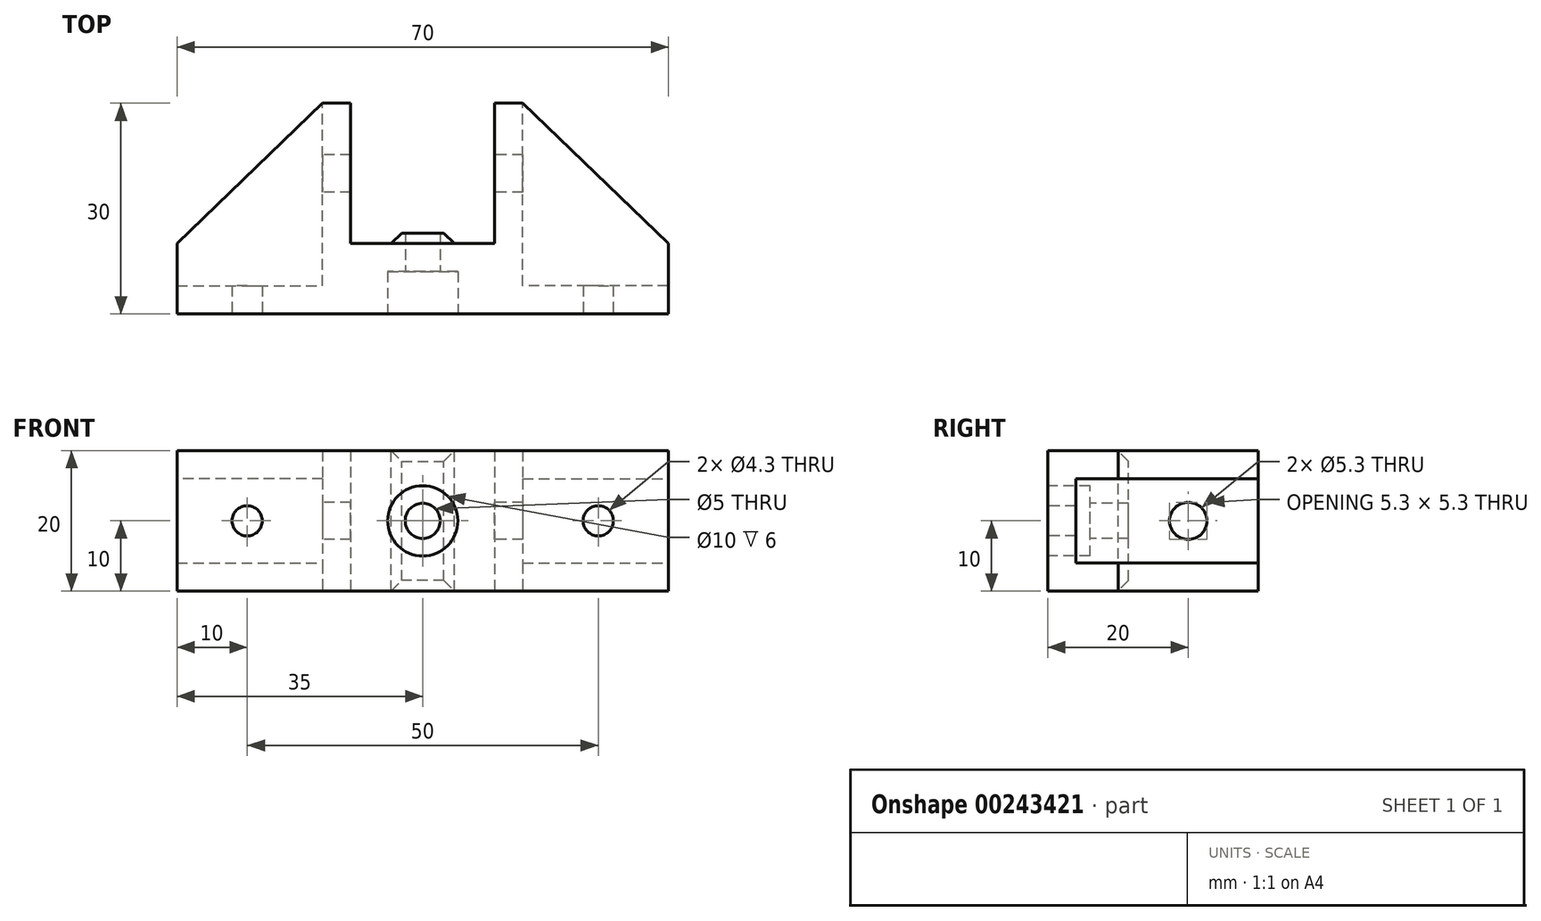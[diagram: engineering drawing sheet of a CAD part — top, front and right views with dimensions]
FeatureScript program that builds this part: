
annotation { "Feature Type Name" : "Feature", "Feature Type Description" : "" }
export const myFeature = defineFeature(function(context is Context, id is Id, definition is map)
    precondition{}
    {
        {
            var Q0;
            Q0=qCreatedBy(makeId("Top.planeOp"),FACE);
            var sketch = newSketch(context, id + "F0", { "sketchPlane" : qUnion([Q0])});
            skLineSegment(sketch, "E0.bottom", {"start": v(0, 0) * mm, "end": v(70, 0) * mm});
            skLineSegment(sketch, "E0.top", {"start": v(0, 10) * mm, "end": v(20.75, 10) * mm});
            skLineSegment(sketch, "E0.left", {"start": v(0, 0) * mm, "end": v(0, 10) * mm});
            skLineSegment(sketch, "E0.right", {"start": v(70, 0) * mm, "end": v(70, 10) * mm});
            skLineSegment(sketch, "E1.top", {"start": v(20.75, 30) * mm, "end": v(24.75, 30) * mm});
            skLineSegment(sketch, "E1.left", {"start": v(20.75, 10) * mm, "end": v(20.75, 30) * mm});
            skLineSegment(sketch, "E1.right", {"start": v(49.25, 10) * mm, "end": v(49.25, 30) * mm});
            skLineSegment(sketch, "E2.trimOffspring", {"start": v(49.25, 10) * mm, "end": v(70, 10) * mm});
            skLineSegment(sketch, "E3.top", {"start": v(24.75, 10) * mm, "end": v(45.25, 10) * mm});
            skLineSegment(sketch, "E3.left", {"start": v(24.75, 30) * mm, "end": v(24.75, 10) * mm});
            skLineSegment(sketch, "E3.right", {"start": v(45.25, 30) * mm, "end": v(45.25, 10) * mm});
            skLineSegment(sketch, "E4.trimOffspring", {"start": v(45.25, 30) * mm, "end": v(49.25, 30) * mm});
            skSolve(sketch);
        }
        {
            var Q0;
            Q0 = qSketchRegion(id + "F0", true);
            extrude(context, id + "F1", {"entities" : qUnion([Q0]), "depth" : 20 * mm});
        }
        {
            var Q0;
            Q0=makeQuery(id+"F1.opExtrude","CAP_FACE",FACE,{"disambiguationData":[OSD([sQuery(id+"F0.wireOp",EDGE,"E0.bottom"),sQuery(id+"F0.wireOp",EDGE,"E0.top"),sQuery(id+"F0.wireOp",EDGE,"E0.left"),sQuery(id+"F0.wireOp",EDGE,"E0.right"),sQuery(id+"F0.wireOp",EDGE,"E1.top"),sQuery(id+"F0.wireOp",EDGE,"E1.left"),sQuery(id+"F0.wireOp",EDGE,"E1.right"),sQuery(id+"F0.wireOp",EDGE,"E2.trimOffspring"),sQuery(id+"F0.wireOp",EDGE,"E3.top"),sQuery(id+"F0.wireOp",EDGE,"E3.left"),sQuery(id+"F0.wireOp",EDGE,"E3.right"),sQuery(id+"F0.wireOp",EDGE,"E4.trimOffspring")])],"isStart":false});
            var sketch = newSketch(context, id + "F2", { "sketchPlane" : qUnion([Q0])});
            skLineSegment(sketch, "E5", {"start": v(30.5, 10) * mm, "end": v(32, 11.5) * mm});
            skLineSegment(sketch, "E6", {"start": v(32, 11.5) * mm, "end": v(38, 11.5) * mm});
            skLineSegment(sketch, "E7", {"start": v(38, 11.5) * mm, "end": v(39.5, 10) * mm});
            skLineSegment(sketch, "E8", {"start": v(39.5, 10) * mm, "end": v(30.5, 10) * mm});
            skSolve(sketch);
        }
        {
            var Q0;
            Q0 = qSketchRegion(id + "F2", true);
            var Q1;
            Q1=makeQuery(id+"F1.opExtrude","CAP_FACE",FACE,{"disambiguationData":[OSD([sQuery(id+"F0.wireOp",EDGE,"E0.bottom"),sQuery(id+"F0.wireOp",EDGE,"E0.top"),sQuery(id+"F0.wireOp",EDGE,"E0.left"),sQuery(id+"F0.wireOp",EDGE,"E0.right"),sQuery(id+"F0.wireOp",EDGE,"E1.top"),sQuery(id+"F0.wireOp",EDGE,"E1.left"),sQuery(id+"F0.wireOp",EDGE,"E1.right"),sQuery(id+"F0.wireOp",EDGE,"E2.trimOffspring"),sQuery(id+"F0.wireOp",EDGE,"E3.top"),sQuery(id+"F0.wireOp",EDGE,"E3.left"),sQuery(id+"F0.wireOp",EDGE,"E3.right"),sQuery(id+"F0.wireOp",EDGE,"E4.trimOffspring")])],"isStart":true});
            extrude(context, id + "F3", {"entities" : qUnion([Q0]), "operationType" : NewBodyOperationType.ADD, "endBound" : BoundingType.UP_TO_SURFACE, "oppositeDirection" : true, "endBoundEntityFace" : qUnion([Q1]), "depth" : 25 * mm});
        }
        {
            var Q0;
            Q0=makeQuery(id+"F1.opExtrude","SWEPT_FACE",FACE,{"disambiguationData":[OSD([sQuery(id+"F0.wireOp",EDGE,"E0.top")])]});
            var sketch = newSketch(context, id + "F4", { "sketchPlane" : qUnion([Q0])});
            skLineSegment(sketch, "E9.bottom", {"start": v(0, 16) * mm, "end": v(-20.75, 16) * mm});
            skLineSegment(sketch, "E9.top", {"start": v(0, 4) * mm, "end": v(-20.75, 4) * mm});
            skLineSegment(sketch, "E9.left", {"start": v(0, 16) * mm, "end": v(0, 4) * mm});
            skLineSegment(sketch, "E9.right", {"start": v(-20.75, 16) * mm, "end": v(-20.75, 4) * mm});
            skLineSegment(sketch, "E10.0.0", {"start": v(-38, 20) * mm, "end": v(-38, 0) * mm, "construction": true});
            skLineSegment(sketch, "E10.0.1", {"start": v(-38, 0) * mm, "end": v(-32, 0) * mm, "construction": true});
            skLineSegment(sketch, "E10.0.2", {"start": v(-32, 0) * mm, "end": v(-32, 20) * mm, "construction": true});
            skLineSegment(sketch, "E10.0.3", {"start": v(-32, 20) * mm, "end": v(-38, 20) * mm, "construction": true});
            skLineSegment(sketch, "E11", {"start": v(-35, 20) * mm, "end": v(-35, 0) * mm, "construction": true});
            skLineSegment(sketch, "E12.MirrorCS", {"start": v(-49.25, 16) * mm, "end": v(-49.25, 4) * mm});
            skLineSegment(sketch, "E13.MirrorCS", {"start": v(-70, 16) * mm, "end": v(-70, 4) * mm});
            skLineSegment(sketch, "E14.MirrorCS", {"start": v(-70, 16) * mm, "end": v(-49.25, 16) * mm});
            skLineSegment(sketch, "E15.MirrorCS", {"start": v(-70, 4) * mm, "end": v(-49.25, 4) * mm});
            skSolve(sketch);
        }
        {
            var Q0;
            Q0 = qSketchRegion(id + "F4", true);
            extrude(context, id + "F5", {"entities" : qUnion([Q0]), "operationType" : NewBodyOperationType.REMOVE, "oppositeDirection" : true, "depth" : 6 * mm});
        }
        {
            var Q0;
            Q0=makeQuery(id+"F3.boolean.opBoolean","MERGE",FACE,{"derivedFrom":[makeQuery(id+"F1.opExtrude","CAP_FACE",FACE,{"disambiguationData":[OSD([sQuery(id+"F0.wireOp",EDGE,"E0.bottom"),sQuery(id+"F0.wireOp",EDGE,"E0.top"),sQuery(id+"F0.wireOp",EDGE,"E0.left"),sQuery(id+"F0.wireOp",EDGE,"E0.right"),sQuery(id+"F0.wireOp",EDGE,"E1.top"),sQuery(id+"F0.wireOp",EDGE,"E1.left"),sQuery(id+"F0.wireOp",EDGE,"E1.right"),sQuery(id+"F0.wireOp",EDGE,"E2.trimOffspring"),sQuery(id+"F0.wireOp",EDGE,"E3.top"),sQuery(id+"F0.wireOp",EDGE,"E3.left"),sQuery(id+"F0.wireOp",EDGE,"E3.right"),sQuery(id+"F0.wireOp",EDGE,"E4.trimOffspring")])],"isStart":true}),makeQuery(id+"F3.opExtrude","CAP_FACE",FACE,{"disambiguationData":[OSD([sQuery(id+"F2.wireOp",EDGE,"E5"),sQuery(id+"F2.wireOp",EDGE,"E6"),sQuery(id+"F2.wireOp",EDGE,"E7"),sQuery(id+"F2.wireOp",EDGE,"E8")])],"isStart":false})]});
            var sketch = newSketch(context, id + "F6", { "sketchPlane" : qUnion([Q0])});
            skLineSegment(sketch, "E16.0", {"start": v(0, -10) * mm, "end": v(20.75, -10) * mm});
            skLineSegment(sketch, "E17.0", {"start": v(20.75, -10) * mm, "end": v(20.75, -30) * mm});
            skLineSegment(sketch, "E18", {"start": v(0, -10) * mm, "end": v(20.75, -30) * mm});
            skLineSegment(sketch, "E19.0", {"start": v(49.25, -10) * mm, "end": v(49.25, -30) * mm});
            skLineSegment(sketch, "E20.0", {"start": v(49.25, -10) * mm, "end": v(70, -10) * mm});
            skLineSegment(sketch, "E21", {"start": v(49.25, -30) * mm, "end": v(70, -10) * mm});
            skSolve(sketch);
        }
        {
            var Q0;
            Q0 = qSketchRegion(id + "F6", true);
            var Q1;
            Q1=makeQuery(id+"F5.boolean.opBoolean","COPY",FACE,{"derivedFrom":makeQuery(id+"F5.opExtrude","SWEPT_FACE",FACE,{"disambiguationData":[OSD([sQuery(id+"F4.wireOp",EDGE,"E9.top")])]})});
            extrude(context, id + "F7", {"entities" : qUnion([Q0]), "operationType" : NewBodyOperationType.ADD, "endBound" : BoundingType.UP_TO_SURFACE, "oppositeDirection" : true, "endBoundEntityFace" : qUnion([Q1]), "depth" : 25 * mm});
        }
        {
            var Q0;
            Q0=makeQuery(id+"F3.boolean.opBoolean","MERGE",FACE,{"derivedFrom":[makeQuery(id+"F1.opExtrude","CAP_FACE",FACE,{"disambiguationData":[OSD([sQuery(id+"F0.wireOp",EDGE,"E0.bottom"),sQuery(id+"F0.wireOp",EDGE,"E0.top"),sQuery(id+"F0.wireOp",EDGE,"E0.left"),sQuery(id+"F0.wireOp",EDGE,"E0.right"),sQuery(id+"F0.wireOp",EDGE,"E1.top"),sQuery(id+"F0.wireOp",EDGE,"E1.left"),sQuery(id+"F0.wireOp",EDGE,"E1.right"),sQuery(id+"F0.wireOp",EDGE,"E2.trimOffspring"),sQuery(id+"F0.wireOp",EDGE,"E3.top"),sQuery(id+"F0.wireOp",EDGE,"E3.left"),sQuery(id+"F0.wireOp",EDGE,"E3.right"),sQuery(id+"F0.wireOp",EDGE,"E4.trimOffspring")])],"isStart":false}),makeQuery(id+"F3.opExtrude","CAP_FACE",FACE,{"disambiguationData":[OSD([sQuery(id+"F2.wireOp",EDGE,"E5"),sQuery(id+"F2.wireOp",EDGE,"E6"),sQuery(id+"F2.wireOp",EDGE,"E7"),sQuery(id+"F2.wireOp",EDGE,"E8")])],"isStart":true})]});
            var sketch = newSketch(context, id + "F8", { "sketchPlane" : qUnion([Q0])});
            skLineSegment(sketch, "E22", {"start": v(0, 10) * mm, "end": v(20.75, 30) * mm});
            skLineSegment(sketch, "E23", {"start": v(20.75, 30) * mm, "end": v(20.75, 10) * mm});
            skLineSegment(sketch, "E24", {"start": v(20.75, 10) * mm, "end": v(0, 10) * mm});
            skLineSegment(sketch, "E25", {"start": v(70, 10) * mm, "end": v(49.25, 30) * mm});
            skLineSegment(sketch, "E26", {"start": v(49.25, 30) * mm, "end": v(49.25, 10) * mm});
            skLineSegment(sketch, "E27", {"start": v(49.25, 10) * mm, "end": v(70, 10) * mm});
            skSolve(sketch);
        }
        {
            var Q0;
            Q0 = qSketchRegion(id + "F8", true);
            var Q1;
            Q1=makeQuery(id+"F5.boolean.opBoolean","COPY",FACE,{"derivedFrom":makeQuery(id+"F5.opExtrude","SWEPT_FACE",FACE,{"disambiguationData":[OSD([sQuery(id+"F4.wireOp",EDGE,"E9.bottom")])]})});
            extrude(context, id + "F9", {"entities" : qUnion([Q0]), "operationType" : NewBodyOperationType.ADD, "endBound" : BoundingType.UP_TO_SURFACE, "oppositeDirection" : true, "endBoundEntityFace" : qUnion([Q1]), "depth" : 25 * mm});
        }
        {
            var Q0;
            Q0=makeQuery(id+"F1.opExtrude","SWEPT_FACE",FACE,{"disambiguationData":[OSD([sQuery(id+"F0.wireOp",EDGE,"E0.bottom")])]});
            var sketch = newSketch(context, id + "F10", { "sketchPlane" : qUnion([Q0])});
            skCircle(sketch, "E28", {"center": v(10, 10) * mm, "radius": 2.15 * mm});
            skPoint(sketch, "E28.centerSnap0", {"position": v(0, 10) * mm});
            skCircle(sketch, "E29", {"center": v(35, 10) * mm, "radius": 2.5 * mm});
            skCircle(sketch, "E30", {"center": v(60, 10) * mm, "radius": 2.15 * mm});
            skSolve(sketch);
        }
        {
            var Q0;
            Q0 = qSketchRegion(id + "F10", true);
            extrude(context, id + "F11", {"entities" : qUnion([Q0]), "operationType" : NewBodyOperationType.REMOVE, "endBound" : BoundingType.THROUGH_ALL, "oppositeDirection" : true, "depth" : 25 * mm});
        }
        {
            var Q0;
            Q0=makeQuery(id+"F1.opExtrude","SWEPT_FACE",FACE,{"disambiguationData":[OSD([sQuery(id+"F0.wireOp",EDGE,"E0.bottom")])]});
            var sketch = newSketch(context, id + "F12", { "sketchPlane" : qUnion([Q0])});
            skCircle(sketch, "E31", {"center": v(35, 10) * mm, "radius": 5 * mm});
            skSolve(sketch);
        }
        {
            var Q0;
            Q0 = qSketchRegion(id + "F12", true);
            extrude(context, id + "F13", {"entities" : qUnion([Q0]), "operationType" : NewBodyOperationType.REMOVE, "oppositeDirection" : true, "depth" : 6 * mm});
        }
        {
            var Q0;
            Q0=makeQuery(id+"F3.opExtrude","CAP_EDGE",EDGE,{"disambiguationData":[OSD([sQuery(id+"F2.wireOp",EDGE,"E6")])],"isStart":true});
            var Q1;
            Q1=makeQuery(id+"F3.opExtrude","CAP_EDGE",EDGE,{"disambiguationData":[OSD([sQuery(id+"F2.wireOp",EDGE,"E6")])],"isStart":false});
            chamfer(context, id + "F14", {"entities" : qUnion([Q0, Q1]), "width" : 1.5 * mm, "tangentPropagation" : true});
        }
        {
            var Q0;
            Q0=makeQuery(id+"F5.boolean.opBoolean","MERGE",FACE,{"derivedFrom":[makeQuery(id+"F1.opExtrude","SWEPT_FACE",FACE,{"disambiguationData":[OSD([sQuery(id+"F0.wireOp",EDGE,"E1.left")])]}),makeQuery(id+"F5.opExtrude","SWEPT_FACE",FACE,{"disambiguationData":[OSD([sQuery(id+"F4.wireOp",EDGE,"E9.right")])]})]});
            var sketch = newSketch(context, id + "F15", { "sketchPlane" : qUnion([Q0])});
            skPoint(sketch, "E32.centerSnap1", {"position": v(-20, 19.5) * mm});
            skCircle(sketch, "E33", {"center": v(-20, 10) * mm, "radius": 2.65 * mm});
            skPoint(sketch, "E33.centerSnap0", {"position": v(-30, 10) * mm});
            skSolve(sketch);
        }
        {
            var Q0;
            Q0 = qSketchRegion(id + "F15", true);
            extrude(context, id + "F16", {"entities" : qUnion([Q0]), "operationType" : NewBodyOperationType.REMOVE, "endBound" : BoundingType.THROUGH_ALL, "oppositeDirection" : true, "depth" : 25 * mm});
        }
    });
